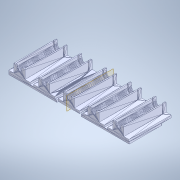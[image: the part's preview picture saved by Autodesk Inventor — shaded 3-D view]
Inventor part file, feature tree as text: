
AUTODESK INVENTOR PART (.ipt)
format: ipt  version: 2022 (Build 260153000, 153)  size: 140,288 bytes
history: native  units: in
note: dims shown in document units (in); Inventor stores cm internally (conversion verified against a paired STEP export)
features: other x2, plane x1
ambient origin geometry x8: Origin, YZ Plane, XZ Plane, XY Plane, X Axis, Y Axis, Z Axis, Center Point
feature tree (3):
  other  "SyringeHolder"
  plane  "Work Plane1"
  other  "Graphic (Closed) -1"
